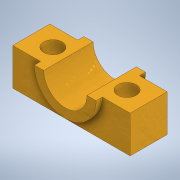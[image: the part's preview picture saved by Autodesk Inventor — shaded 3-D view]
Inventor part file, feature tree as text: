
AUTODESK INVENTOR PART (.ipt)
format: ipt  version: 2020 (Build 240168000, 168)  size: 138,752 bytes
history: native  units: mm
features: sketch x4, extrude x2, hole x2
ambient origin geometry x8: Origin, YZ Plane, XZ Plane, XY Plane, X Axis, Y Axis, Z Axis, Center Point
bodies: Solid1 (feature_tree)
feature tree (8):
  extrude  "Extrusion1"  Depth=6.0mm
  extrude  "Extrusion2"  Depth=5.0mm
  hole  "Hole1"  [1 undecoded]
  hole  "Hole2"  [1 undecoded]
  sketch  "Sketch1"  dims[d0=19.0mm d1=6.0mm]
  sketch  "Sketch2"  dims[d2=6.0mm d3=0.0mm d4=5.0mm]
  sketch  "Sketch3"  dims[d5=1.0mm d6=7.0mm d7=0.0mm d8=0.0mm]
  sketch  "Sketch4"  dims[d9=7.0mm d10=6.0mm d11=4.0mm d12=2.0mm d13=90.0deg d14=8.0mm d15=20.594885mm d16=3.0mm d17=3.0mm d18=12.0mm d19=3.5mm d20=3.5mm d21=3.0mm d22=6.0mm d23=4.0mm d24=2.0mm d25=90.0deg d26=8.0mm d27=20.594885mm]
note: 2 required parameter values undecoded (feature->parameter linkage not recoverable at this tier; creation-order binding heuristic only, values carry confidence <= 0.55)
